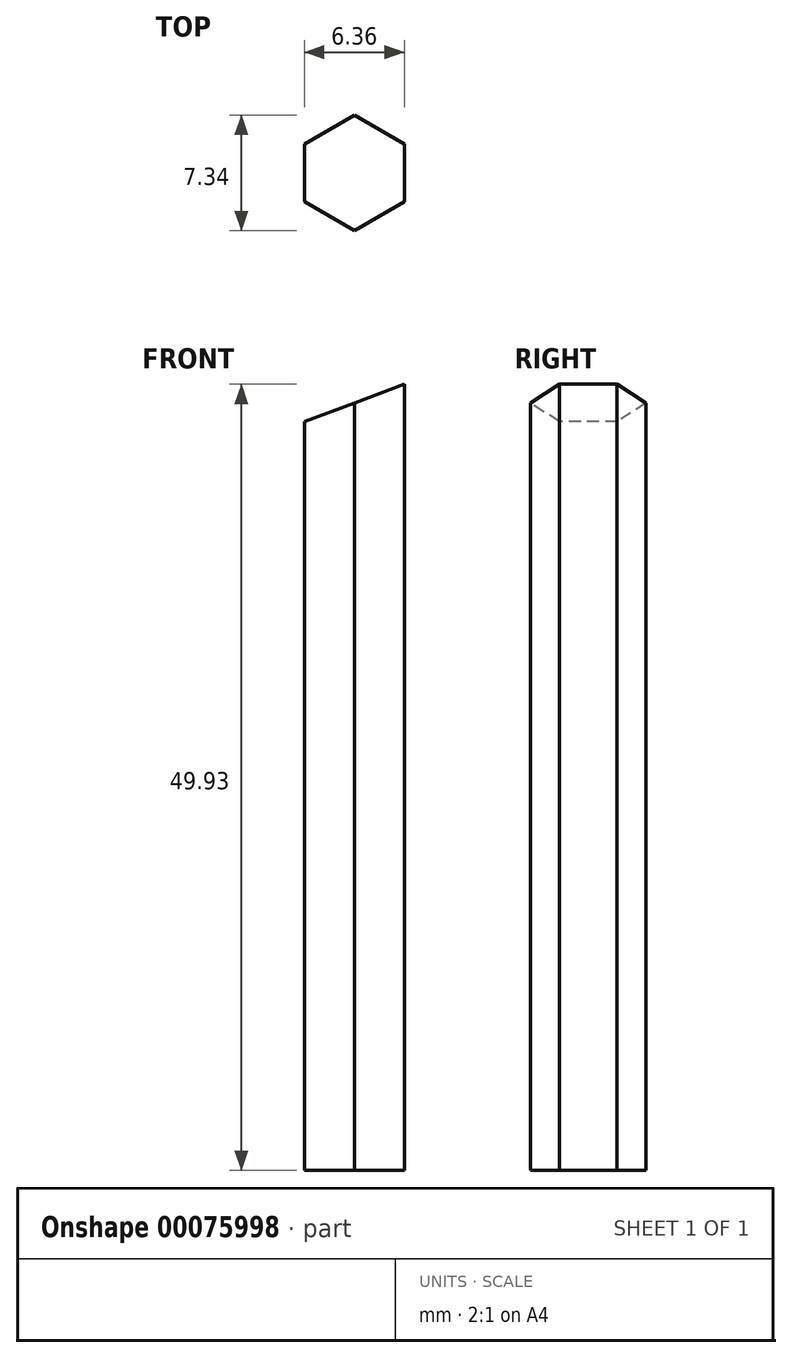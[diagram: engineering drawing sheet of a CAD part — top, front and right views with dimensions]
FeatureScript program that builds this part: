
annotation { "Feature Type Name" : "Feature", "Feature Type Description" : "" }
export const myFeature = defineFeature(function(context is Context, id is Id, definition is map)
    precondition{}
    {
        {
            var Q0;
            Q0=qCreatedBy(makeId("Top.planeOp"),FACE);
            var sketch = newSketch(context, id + "F0", { "sketchPlane" : qUnion([Q0])});
            skCircle(sketch, "E0.cCircle", {"center": v(0, 0) * mm, "radius": 3.18 * mm, "construction": true});
            skLineSegment(sketch, "E0.0", {"start": v(-3.18, 1.83) * mm, "end": v(0, 3.67) * mm});
            skLineSegment(sketch, "E0.1", {"start": v(0, 3.67) * mm, "end": v(3.17, 1.83) * mm});
            skLineSegment(sketch, "E0.2", {"start": v(3.18, 1.83) * mm, "end": v(3.18, -1.83) * mm});
            skLineSegment(sketch, "E0.3", {"start": v(3.18, -1.83) * mm, "end": v(0, -3.67) * mm});
            skLineSegment(sketch, "E0.4", {"start": v(0, -3.67) * mm, "end": v(-3.18, -1.83) * mm});
            skLineSegment(sketch, "E0.5", {"start": v(-3.18, -1.83) * mm, "end": v(-3.18, 1.83) * mm});
            skPoint(sketch, "E0.0.midPoint", {"position": v(-1.59, 2.75) * mm});
            skSolve(sketch);
        }
        {
            var Q0;
            Q0 = qSketchRegion(id + "F0", true);
            extrude(context, id + "F1", {"entities" : qUnion([Q0]), "depth" : 50.8 * mm});
        }
        {
            var Q0;
            Q0=qCreatedBy(makeId("Front.planeOp"),FACE);
            var sketch = newSketch(context, id + "F2", { "sketchPlane" : qUnion([Q0])});
            skLineSegment(sketch, "E1", {"start": v(-6.18, 46.43) * mm, "end": v(5.68, 50.86) * mm});
            skLineSegment(sketch, "E2", {"start": v(5.68, 54.1) * mm, "end": v(-6.35, 54.1) * mm});
            skLineSegment(sketch, "E3", {"start": v(-6.35, 54.1) * mm, "end": v(-6.18, 46.43) * mm});
            skLineSegment(sketch, "E4", {"start": v(5.68, 54.1) * mm, "end": v(5.68, 50.86) * mm});
            skSolve(sketch);
        }
        {
            var Q0;
            Q0 = qSketchRegion(id + "F2", true);
            extrude(context, id + "F3", {"entities" : qUnion([Q0]), "operationType" : NewBodyOperationType.REMOVE, "endBound" : BoundingType.SYMMETRIC, "oppositeDirection" : true, "depth" : 25.4 * mm});
        }
    });
